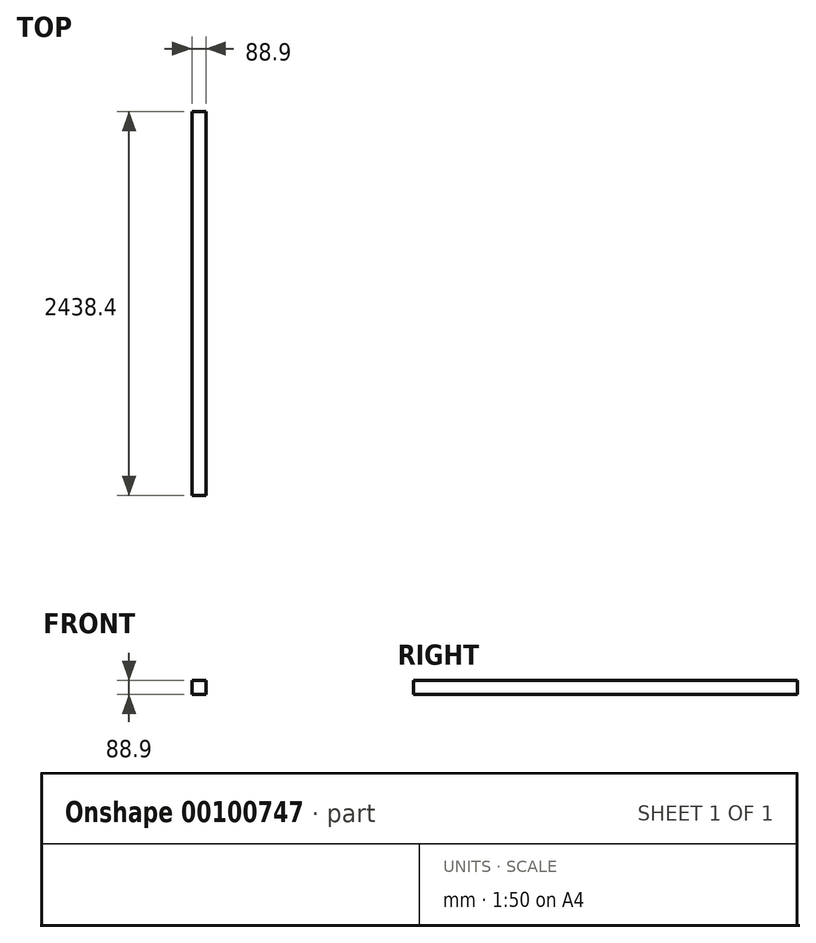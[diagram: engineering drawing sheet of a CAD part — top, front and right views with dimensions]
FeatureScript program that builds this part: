
annotation { "Feature Type Name" : "Feature", "Feature Type Description" : "" }
export const myFeature = defineFeature(function(context is Context, id is Id, definition is map)
    precondition{}
    {
        {
            var Q0;
            Q0=qCreatedBy(makeId("Front.planeOp"),FACE);
            var sketch = newSketch(context, id + "F0", { "sketchPlane" : qUnion([Q0])});
            skLineSegment(sketch, "E0.bottom", {"start": v(0, 0) * mm, "end": v(88.9, 0) * mm});
            skLineSegment(sketch, "E0.top", {"start": v(0, 88.9) * mm, "end": v(88.9, 88.9) * mm});
            skLineSegment(sketch, "E0.left", {"start": v(0, 0) * mm, "end": v(0, 88.9) * mm});
            skLineSegment(sketch, "E0.right", {"start": v(88.9, 0) * mm, "end": v(88.9, 88.9) * mm});
            skSolve(sketch);
        }
        {
            var Q0;
            Q0=makeQuery(id+"F0.imprint","IMPRINT",FACE,{"disambiguationData":[TD([[makeQuery(id+"F0.imprint","IMPRINT",EDGE,{"derivedFrom":sQuery(id+"F0.wireOp",EDGE,"E0.bottom")}),1.0]])]});
            extrude(context, id + "F1", {"entities" : qUnion([Q0]), "depth" : 2438.4 * mm});
        }
    });
